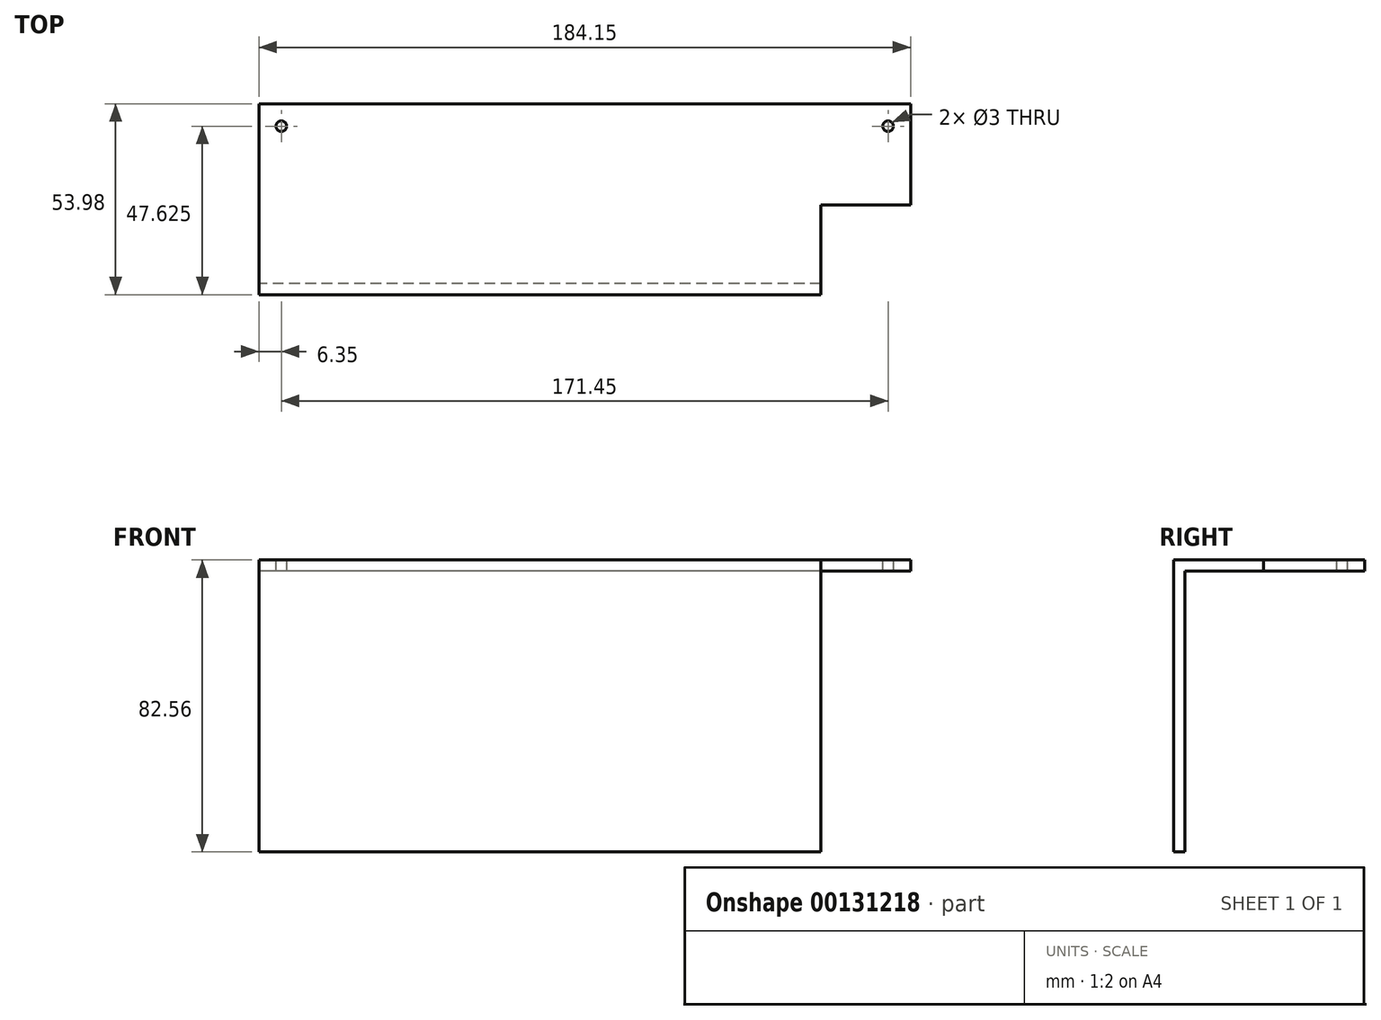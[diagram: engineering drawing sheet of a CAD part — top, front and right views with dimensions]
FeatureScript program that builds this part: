
annotation { "Feature Type Name" : "Feature", "Feature Type Description" : "" }
export const myFeature = defineFeature(function(context is Context, id is Id, definition is map)
    precondition{}
    {
        {
            var Q0;
            Q0=qCreatedBy(makeId("Top.planeOp"),FACE);
            var sketch = newSketch(context, id + "F0", { "sketchPlane" : qUnion([Q0])});
            skLineSegment(sketch, "E0.bottom", {"start": v(0, 0) * mm, "end": v(-184.15, 0) * mm});
            skLineSegment(sketch, "E0.top", {"start": v(0, 53.97) * mm, "end": v(-184.15, 53.97) * mm});
            skLineSegment(sketch, "E0.left", {"start": v(0, 0) * mm, "end": v(0, 53.97) * mm});
            skLineSegment(sketch, "E0.right", {"start": v(-184.15, 0) * mm, "end": v(-184.15, 53.97) * mm});
            skSolve(sketch);
        }
        {
            var Q0;
            Q0=makeQuery(id+"F0.imprint","IMPRINT",FACE,{"disambiguationData":[TD([[makeQuery(id+"F0.imprint","IMPRINT",EDGE,{"derivedFrom":sQuery(id+"F0.wireOp",EDGE,"E0.bottom")}),-1.0]])]});
            extrude(context, id + "F1", {"entities" : qUnion([Q0]), "depth" : 3.17 * mm});
        }
        {
            var Q0;
            Q0=makeQuery(id+"F1.opExtrude","CAP_FACE",FACE,{"disambiguationData":[OSD([sQuery(id+"F0.wireOp",EDGE,"E0.bottom"),sQuery(id+"F0.wireOp",EDGE,"E0.top"),sQuery(id+"F0.wireOp",EDGE,"E0.left"),sQuery(id+"F0.wireOp",EDGE,"E0.right")])],"isStart":false});
            var sketch = newSketch(context, id + "F2", { "sketchPlane" : qUnion([Q0])});
            skPoint(sketch, "E1", {"position": v(-177.8, 47.62) * mm});
            skPoint(sketch, "E2", {"position": v(-6.35, 47.62) * mm});
            skSolve(sketch);
        }
        {
            var Q0;
            Q0=sQuery(id+"F2.wireOp",VERTEX,"E1");
            var Q1;
            Q1=sQuery(id+"F2.wireOp",VERTEX,"E2");
            var Q2;
            Q2=makeQuery(id+"F1.opExtrude","SWEPT_BODY",BODY,{"disambiguationData":[OSD([sQuery(id+"F0.wireOp",EDGE,"E0.bottom"),sQuery(id+"F0.wireOp",EDGE,"E0.top"),sQuery(id+"F0.wireOp",EDGE,"E0.left"),sQuery(id+"F0.wireOp",EDGE,"E0.right")])]});
            hole(context, id + "F3", {"style" : HoleStyle.SIMPLE, "endStyle" : HoleEndStyle.THROUGH, "holeDiameter" : 3 * mm, "locations" : qUnion([Q0, Q1]), "scope" : qUnion([Q2]), "isTappedThrough" : true});
        }
        {
            var Q0;
            Q0=makeQuery(id+"F1.opExtrude","CAP_FACE",FACE,{"disambiguationData":[OSD([sQuery(id+"F0.wireOp",EDGE,"E0.bottom"),sQuery(id+"F0.wireOp",EDGE,"E0.top"),sQuery(id+"F0.wireOp",EDGE,"E0.left"),sQuery(id+"F0.wireOp",EDGE,"E0.right")])],"isStart":false});
            var sketch = newSketch(context, id + "F4", { "sketchPlane" : qUnion([Q0])});
            skLineSegment(sketch, "E3.bottom", {"start": v(0, 0) * mm, "end": v(-25.4, 0) * mm});
            skLineSegment(sketch, "E3.top", {"start": v(0, 25.4) * mm, "end": v(-25.4, 25.4) * mm});
            skLineSegment(sketch, "E3.left", {"start": v(0, 0) * mm, "end": v(0, 25.4) * mm});
            skLineSegment(sketch, "E3.right", {"start": v(-25.4, 0) * mm, "end": v(-25.4, 25.4) * mm});
            skSolve(sketch);
        }
        {
            var Q0;
            Q0=makeQuery(id+"F4.imprint","IMPRINT",FACE,{"disambiguationData":[TD([[makeQuery(id+"F4.imprint","IMPRINT",EDGE,{"derivedFrom":sQuery(id+"F4.wireOp",EDGE,"E3.bottom")}),-1.0]])]});
            extrude(context, id + "F5", {"entities" : qUnion([Q0]), "operationType" : NewBodyOperationType.REMOVE, "oppositeDirection" : true, "depth" : 25.4 * mm});
        }
        {
            var Q0;
            Q0=makeQuery(id+"F1.opExtrude","CAP_FACE",FACE,{"disambiguationData":[OSD([sQuery(id+"F0.wireOp",EDGE,"E0.bottom"),sQuery(id+"F0.wireOp",EDGE,"E0.top"),sQuery(id+"F0.wireOp",EDGE,"E0.left"),sQuery(id+"F0.wireOp",EDGE,"E0.right")])],"isStart":true});
            var sketch = newSketch(context, id + "F6", { "sketchPlane" : qUnion([Q0])});
            skLineSegment(sketch, "E4.bottom", {"start": v(-25.4, 0) * mm, "end": v(-184.15, 0) * mm});
            skLineSegment(sketch, "E4.top", {"start": v(-25.4, -3.18) * mm, "end": v(-184.15, -3.18) * mm});
            skLineSegment(sketch, "E4.left", {"start": v(-25.4, 0) * mm, "end": v(-25.4, -3.18) * mm});
            skLineSegment(sketch, "E4.right", {"start": v(-184.15, 0) * mm, "end": v(-184.15, -3.18) * mm});
            skSolve(sketch);
        }
        {
            var Q0;
            Q0 = qSketchRegion(id + "F6", true);
            extrude(context, id + "F7", {"entities" : qUnion([Q0]), "operationType" : NewBodyOperationType.ADD, "depth" : 79.38 * mm});
        }
    });
